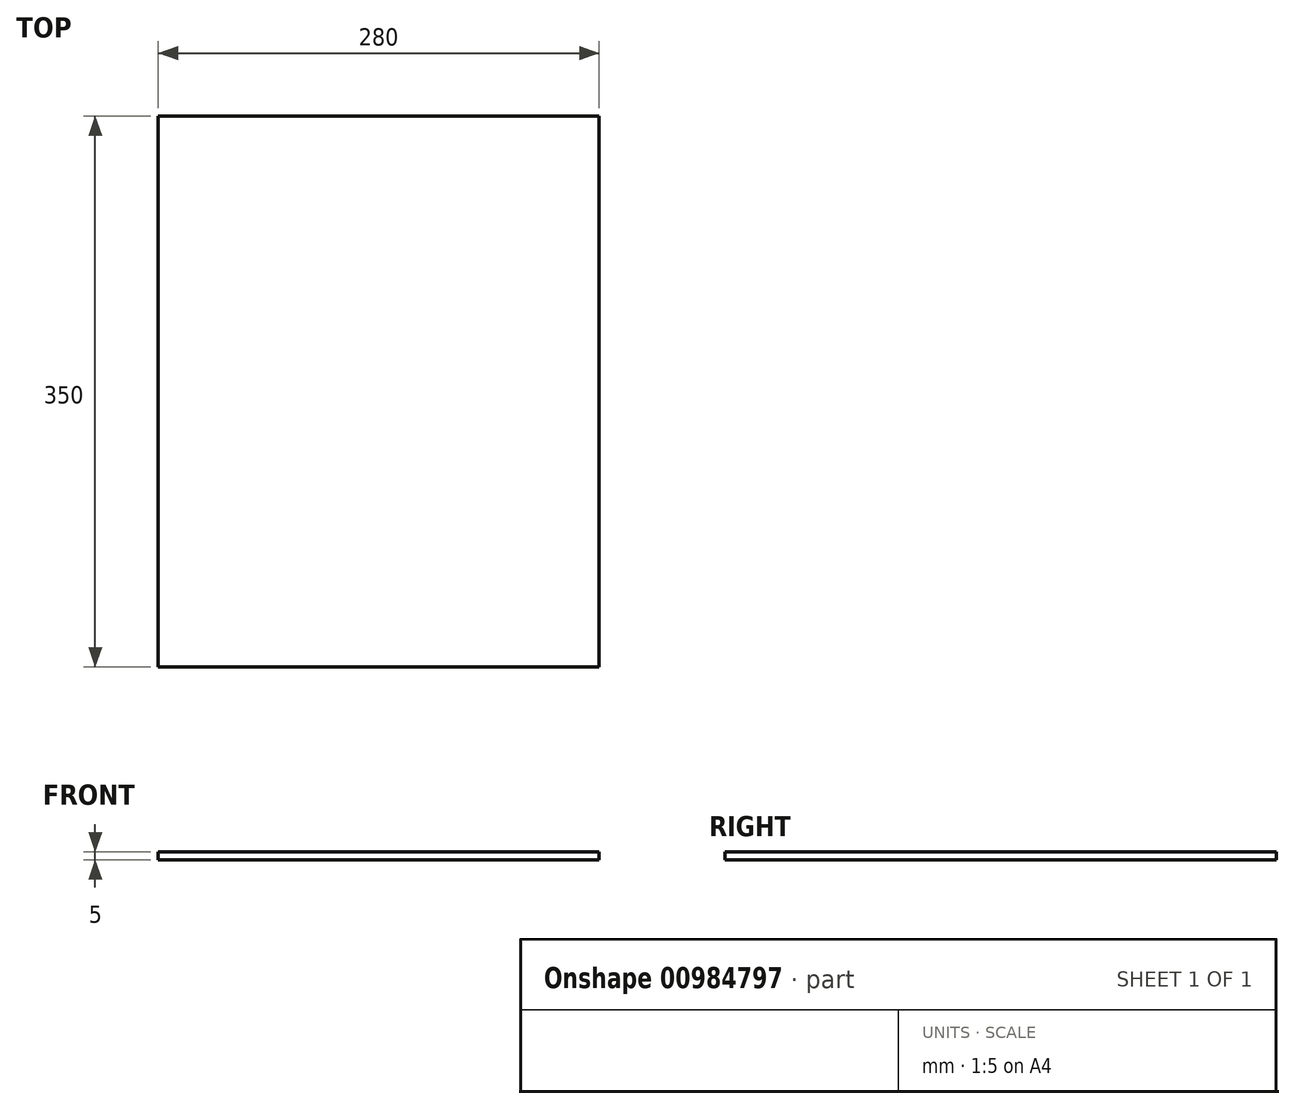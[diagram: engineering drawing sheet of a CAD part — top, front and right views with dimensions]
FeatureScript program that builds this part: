
annotation { "Feature Type Name" : "Feature", "Feature Type Description" : "" }
export const myFeature = defineFeature(function(context is Context, id is Id, definition is map)
    precondition{}
    {
        {
            var Q0;
            Q0=qCreatedBy(makeId("Top.planeOp"),FACE);
            var sketch = newSketch(context, id + "F0", { "sketchPlane" : qUnion([Q0])});
            skLineSegment(sketch, "E0.bottom", {"start": v(140, 175) * mm, "end": v(-140, 175) * mm});
            skLineSegment(sketch, "E0.top", {"start": v(140, -175) * mm, "end": v(-140, -175) * mm});
            skLineSegment(sketch, "E0.left", {"start": v(140, 175) * mm, "end": v(140, -175) * mm});
            skLineSegment(sketch, "E0.right", {"start": v(-140, 175) * mm, "end": v(-140, -175) * mm});
            skPoint(sketch, "E0.middle", {"position": v(0, 0) * mm});
            skSolve(sketch);
        }
        {
            var Q0;
            Q0=makeQuery(id+"F0.imprint","IMPRINT",FACE,{"disambiguationData":[TD([[makeQuery(id+"F0.imprint","IMPRINT",EDGE,{"derivedFrom":sQuery(id+"F0.wireOp",EDGE,"E0.bottom")}),1.0]])]});
            extrude(context, id + "F1", {"entities" : qUnion([Q0]), "depth" : 5 * mm, "offsetDistance" : 25 * mm});
        }
    });
